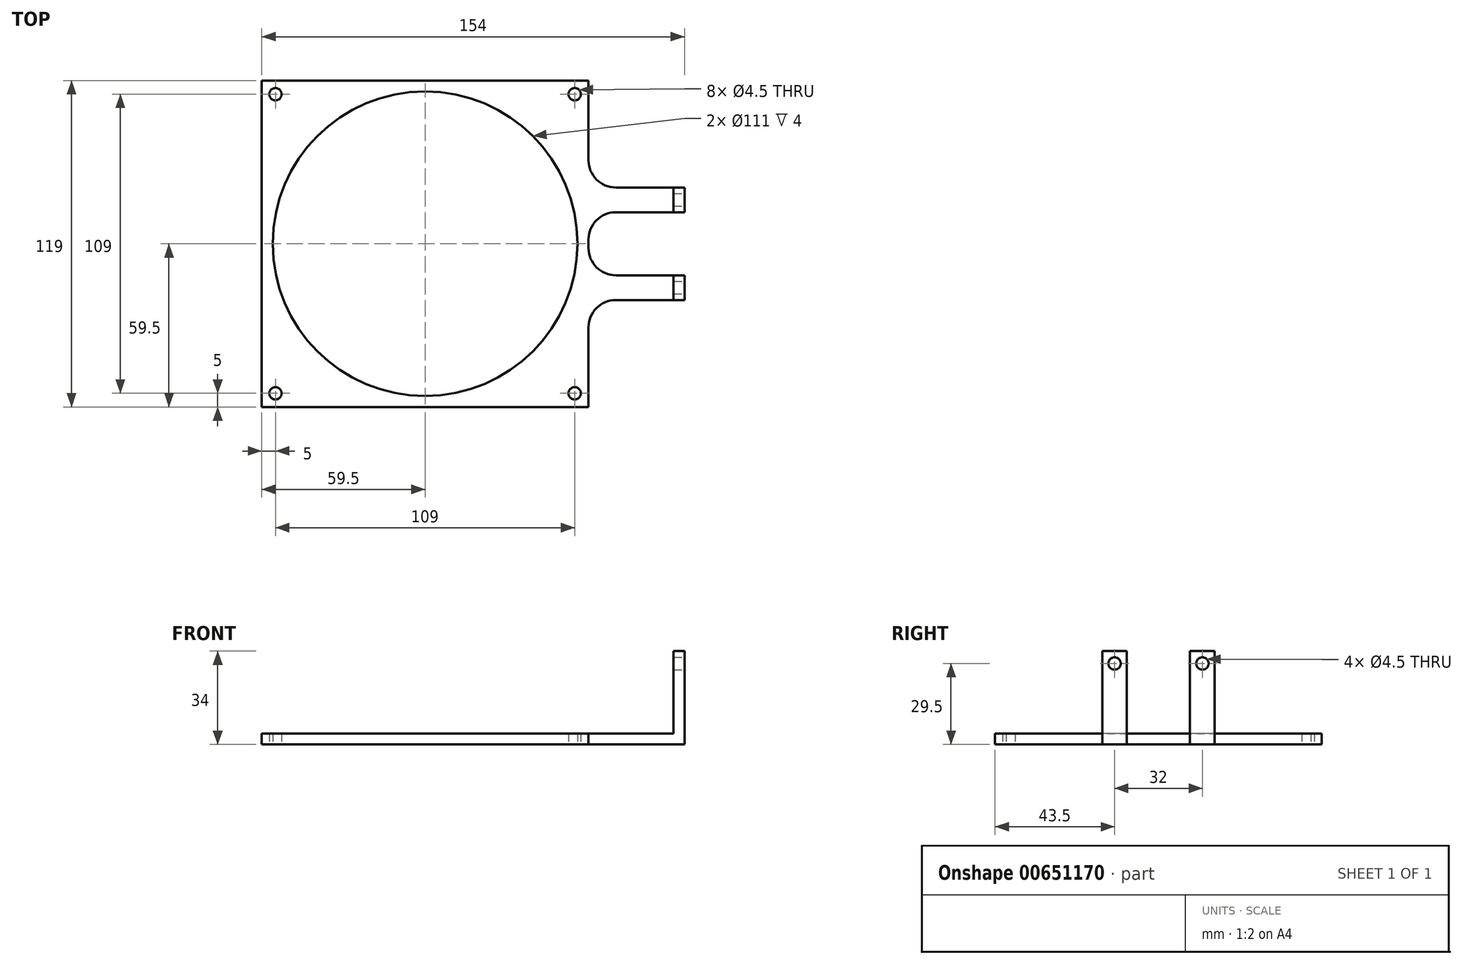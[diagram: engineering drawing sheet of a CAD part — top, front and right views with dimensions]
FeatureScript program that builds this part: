
annotation { "Feature Type Name" : "Feature", "Feature Type Description" : "" }
export const myFeature = defineFeature(function(context is Context, id is Id, definition is map)
    precondition{}
    {
        {
            var Q0;
            Q0=qCreatedBy(makeId("Top.planeOp"),FACE);
            var sketch = newSketch(context, id + "F0", { "sketchPlane" : qUnion([Q0])});
            skCircle(sketch, "E0", {"center": v(54.5, 54.5) * mm, "radius": 2.25 * mm});
            skCircle(sketch, "E1", {"center": v(-54.5, 54.5) * mm, "radius": 2.25 * mm});
            skCircle(sketch, "E2", {"center": v(-54.5, -54.5) * mm, "radius": 2.25 * mm});
            skCircle(sketch, "E3", {"center": v(54.5, -54.5) * mm, "radius": 2.25 * mm});
            skLineSegment(sketch, "E4.bottom", {"start": v(-54.5, 54.5) * mm, "end": v(54.5, 54.5) * mm, "construction": true});
            skLineSegment(sketch, "E4.top", {"start": v(-54.5, -54.5) * mm, "end": v(54.5, -54.5) * mm, "construction": true});
            skLineSegment(sketch, "E4.left", {"start": v(-54.5, 54.5) * mm, "end": v(-54.5, -54.5) * mm, "construction": true});
            skLineSegment(sketch, "E4.right", {"start": v(54.5, 54.5) * mm, "end": v(54.5, -54.5) * mm, "construction": true});
            skPoint(sketch, "E4.middle", {"position": v(0, 0) * mm});
            skLineSegment(sketch, "E5.bottom", {"start": v(-59.5, 59.5) * mm, "end": v(59.5, 59.5) * mm});
            skLineSegment(sketch, "E5.top", {"start": v(-59.5, -59.5) * mm, "end": v(59.5, -59.5) * mm});
            skLineSegment(sketch, "E5.left", {"start": v(-59.5, 59.5) * mm, "end": v(-59.5, -59.5) * mm});
            skLineSegment(sketch, "E5.right", {"start": v(59.5, 59.5) * mm, "end": v(59.5, -59.5) * mm});
            skLineSegment(sketch, "E6", {"start": v(0, 0) * mm, "end": v(218.42, 0) * mm, "construction": true});
            skLineSegment(sketch, "E7", {"start": v(59.5, 20.5) * mm, "end": v(94.5, 20.5) * mm});
            skLineSegment(sketch, "E8", {"start": v(94.5, 20.5) * mm, "end": v(94.5, 11.5) * mm});
            skLineSegment(sketch, "E9", {"start": v(94.5, 11.5) * mm, "end": v(59.5, 11.5) * mm});
            skLineSegment(sketch, "E10.MirrorCS", {"start": v(94.5, -11.5) * mm, "end": v(59.5, -11.5) * mm});
            skLineSegment(sketch, "E11.MirrorCS", {"start": v(59.5, -20.5) * mm, "end": v(94.5, -20.5) * mm});
            skLineSegment(sketch, "E12.MirrorCS", {"start": v(94.5, -20.5) * mm, "end": v(94.5, -11.5) * mm});
            skCircle(sketch, "E13", {"center": v(90, 16) * mm, "radius": 4.5 * mm, "construction": true});
            skCircle(sketch, "E14.MirrorC", {"center": v(90, -16) * mm, "radius": 4.5 * mm, "construction": true});
            skCircle(sketch, "E15", {"center": v(0, 0) * mm, "radius": 55.5 * mm});
            skSolve(sketch);
        }
        {
            var Q0;
            Q0=makeQuery(id+"F0.imprint","IMPRINT",FACE,{"disambiguationData":[TD([[makeQuery(id+"F0.imprint","IMPRINT",EDGE,{"derivedFrom":sQuery(id+"F0.wireOp",EDGE,"E0")}),-1.0]])]});
            var Q1;
            {var subQ0=sQuery(id+"F0.wireOp",EDGE,"E10.MirrorCS");Q1=makeQuery(id+"F0.imprint","IMPRINT",FACE,{"disambiguationData":[TD([[makeQuery(id+"F0.imprint","IMPRINT",EDGE,{"derivedFrom":subQ0}),1.0]])]});}
            var Q2;
            {var subQ0=sQuery(id+"F0.wireOp",EDGE,"E7");Q2=makeQuery(id+"F0.imprint","IMPRINT",FACE,{"disambiguationData":[TD([[makeQuery(id+"F0.imprint","IMPRINT",EDGE,{"derivedFrom":subQ0}),-1.0]])]});}
            extrude(context, id + "F1", {"entities" : qUnion([Q0, Q1, Q2]), "depth" : 4 * mm, "offsetDistance" : 25 * mm});
        }
        {
            var Q0;
            Q0=makeQuery(id+"F1.opExtrude","CAP_FACE",FACE,{"disambiguationData":[OSD([sQuery(id+"F0.wireOp",EDGE,"E0"),sQuery(id+"F0.wireOp",EDGE,"E1"),sQuery(id+"F0.wireOp",EDGE,"E2"),sQuery(id+"F0.wireOp",EDGE,"E3"),sQuery(id+"F0.wireOp",EDGE,"E5.bottom"),sQuery(id+"F0.wireOp",EDGE,"E5.top"),sQuery(id+"F0.wireOp",EDGE,"E5.left"),sQuery(id+"F0.wireOp",EDGE,"E5.right"),sQuery(id+"F0.wireOp",EDGE,"E7"),sQuery(id+"F0.wireOp",EDGE,"E8"),sQuery(id+"F0.wireOp",EDGE,"E9"),sQuery(id+"F0.wireOp",EDGE,"E10.MirrorCS"),sQuery(id+"F0.wireOp",EDGE,"E11.MirrorCS"),sQuery(id+"F0.wireOp",EDGE,"E12.MirrorCS"),sQuery(id+"F0.wireOp",EDGE,"E15")])],"isStart":false});
            var sketch = newSketch(context, id + "F2", { "sketchPlane" : qUnion([Q0])});
            skLineSegment(sketch, "E16.bottom", {"start": v(94.5, 20.5) * mm, "end": v(90.5, 20.5) * mm});
            skLineSegment(sketch, "E16.top", {"start": v(94.5, 11.5) * mm, "end": v(90.5, 11.5) * mm});
            skLineSegment(sketch, "E16.left", {"start": v(94.5, 20.5) * mm, "end": v(94.5, 11.5) * mm});
            skLineSegment(sketch, "E16.right", {"start": v(90.5, 20.5) * mm, "end": v(90.5, 11.5) * mm});
            skLineSegment(sketch, "E17.bottom", {"start": v(94.5, -11.5) * mm, "end": v(90.5, -11.5) * mm});
            skLineSegment(sketch, "E17.top", {"start": v(94.5, -20.5) * mm, "end": v(90.5, -20.5) * mm});
            skLineSegment(sketch, "E17.left", {"start": v(94.5, -11.5) * mm, "end": v(94.5, -20.5) * mm});
            skLineSegment(sketch, "E17.right", {"start": v(90.5, -11.5) * mm, "end": v(90.5, -20.5) * mm});
            skSolve(sketch);
        }
        {
            var Q0;
            Q0=makeQuery(id+"F2.imprint","IMPRINT",FACE,{"disambiguationData":[TD([[makeQuery(id+"F2.imprint","IMPRINT",EDGE,{"derivedFrom":sQuery(id+"F2.wireOp",EDGE,"E16.bottom")}),-1.0]])]});
            var Q1;
            Q1=makeQuery(id+"F2.imprint","IMPRINT",FACE,{"disambiguationData":[TD([[makeQuery(id+"F2.imprint","IMPRINT",EDGE,{"derivedFrom":sQuery(id+"F2.wireOp",EDGE,"E17.bottom")}),1.0]])]});
            extrude(context, id + "F3", {"entities" : qUnion([Q0, Q1]), "operationType" : NewBodyOperationType.ADD, "depth" : 30 * mm, "offsetDistance" : 25 * mm});
        }
        {
            var Q0;
            Q0=makeQuery(id+"F3.boolean.opBoolean","MERGE",FACE,{"derivedFrom":[makeQuery(id+"F1.opExtrude","SWEPT_FACE",FACE,{"disambiguationData":[OSD([sQuery(id+"F0.wireOp",EDGE,"E8")])]}),makeQuery(id+"F3.opExtrude","SWEPT_FACE",FACE,{"disambiguationData":[OSD([sQuery(id+"F2.wireOp",EDGE,"E16.left")])]})]});
            var sketch = newSketch(context, id + "F4", { "sketchPlane" : qUnion([Q0])});
            skCircle(sketch, "E18", {"center": v(-16, 29.5) * mm, "radius": 4.5 * mm, "construction": true});
            skCircle(sketch, "E19", {"center": v(16, 29.5) * mm, "radius": 4.5 * mm, "construction": true});
            skCircle(sketch, "E20", {"center": v(-16, 29.5) * mm, "radius": 2.25 * mm});
            skCircle(sketch, "E21", {"center": v(16, 29.5) * mm, "radius": 2.25 * mm});
            skSolve(sketch);
        }
        {
            var Q0;
            Q0=makeQuery(id+"F4.imprint","IMPRINT",FACE,{"disambiguationData":[TD([[makeQuery(id+"F4.imprint","IMPRINT",EDGE,{"derivedFrom":sQuery(id+"F4.wireOp",EDGE,"E20")}),1.0]])]});
            var Q1;
            Q1=makeQuery(id+"F4.imprint","IMPRINT",FACE,{"disambiguationData":[TD([[makeQuery(id+"F4.imprint","IMPRINT",EDGE,{"derivedFrom":sQuery(id+"F4.wireOp",EDGE,"E21")}),1.0]])]});
            extrude(context, id + "F5", {"entities" : qUnion([Q0, Q1]), "operationType" : NewBodyOperationType.REMOVE, "endBound" : BoundingType.THROUGH_ALL, "oppositeDirection" : true, "depth" : 25 * mm, "offsetDistance" : 25 * mm});
        }
        {
            var Q0;
            Q0=makeQuery(id+"F3.opExtrude","CAP_EDGE",EDGE,{"disambiguationData":[OSD([sQuery(id+"F2.wireOp",EDGE,"E17.right")])],"isStart":true});
            var Q1;
            Q1=makeQuery(id+"F3.opExtrude","CAP_EDGE",EDGE,{"disambiguationData":[OSD([sQuery(id+"F2.wireOp",EDGE,"E16.right")])],"isStart":true});
            var Q2;
            Q2=makeQuery(id+"F1.opExtrude","SWEPT_EDGE",EDGE,{"disambiguationData":[OSD([sQuery(id+"F0.wireOp",EDGE,"E5.right"),sQuery(id+"F0.wireOp",EDGE,"E10.MirrorCS")])]});
            var Q3;
            Q3=makeQuery(id+"F1.opExtrude","SWEPT_EDGE",EDGE,{"disambiguationData":[OSD([sQuery(id+"F0.wireOp",EDGE,"E5.right"),sQuery(id+"F0.wireOp",EDGE,"E7")])]});
            var Q4;
            Q4=makeQuery(id+"F1.opExtrude","SWEPT_EDGE",EDGE,{"disambiguationData":[OSD([sQuery(id+"F0.wireOp",EDGE,"E5.right"),sQuery(id+"F0.wireOp",EDGE,"E9")])]});
            var Q5;
            Q5=makeQuery(id+"F1.opExtrude","SWEPT_EDGE",EDGE,{"disambiguationData":[OSD([sQuery(id+"F0.wireOp",EDGE,"E5.right"),sQuery(id+"F0.wireOp",EDGE,"E11.MirrorCS")])]});
            fillet(context, id + "F6", {"entities" : qUnion([Q0, Q1, Q2, Q3, Q4, Q5]), "radius" : 10 * mm, "tangentPropagation" : true, "allowEdgeOverflow" : false});
        }
        {
            var Q0;
            Q0=makeQuery(id+"F1.opExtrude","SWEPT_BODY",BODY,{"disambiguationData":[OSD([sQuery(id+"F0.wireOp",EDGE,"E0"),sQuery(id+"F0.wireOp",EDGE,"E1"),sQuery(id+"F0.wireOp",EDGE,"E2"),sQuery(id+"F0.wireOp",EDGE,"E3"),sQuery(id+"F0.wireOp",EDGE,"E5.bottom"),sQuery(id+"F0.wireOp",EDGE,"E5.top"),sQuery(id+"F0.wireOp",EDGE,"E5.left"),sQuery(id+"F0.wireOp",EDGE,"E5.right"),sQuery(id+"F0.wireOp",EDGE,"E7"),sQuery(id+"F0.wireOp",EDGE,"E8"),sQuery(id+"F0.wireOp",EDGE,"E9"),sQuery(id+"F0.wireOp",EDGE,"E10.MirrorCS"),sQuery(id+"F0.wireOp",EDGE,"E11.MirrorCS"),sQuery(id+"F0.wireOp",EDGE,"E12.MirrorCS"),sQuery(id+"F0.wireOp",EDGE,"E15")])]});
            transform(context, id + "F7", {"entities" : qUnion([Q0]), "transformType" : TransformType.TRANSLATION_3D, "dx" : 0 * mm, "dy" : 0 * mm, "dz" : 0 * mm, "makeCopy" : true});
        }
    });
